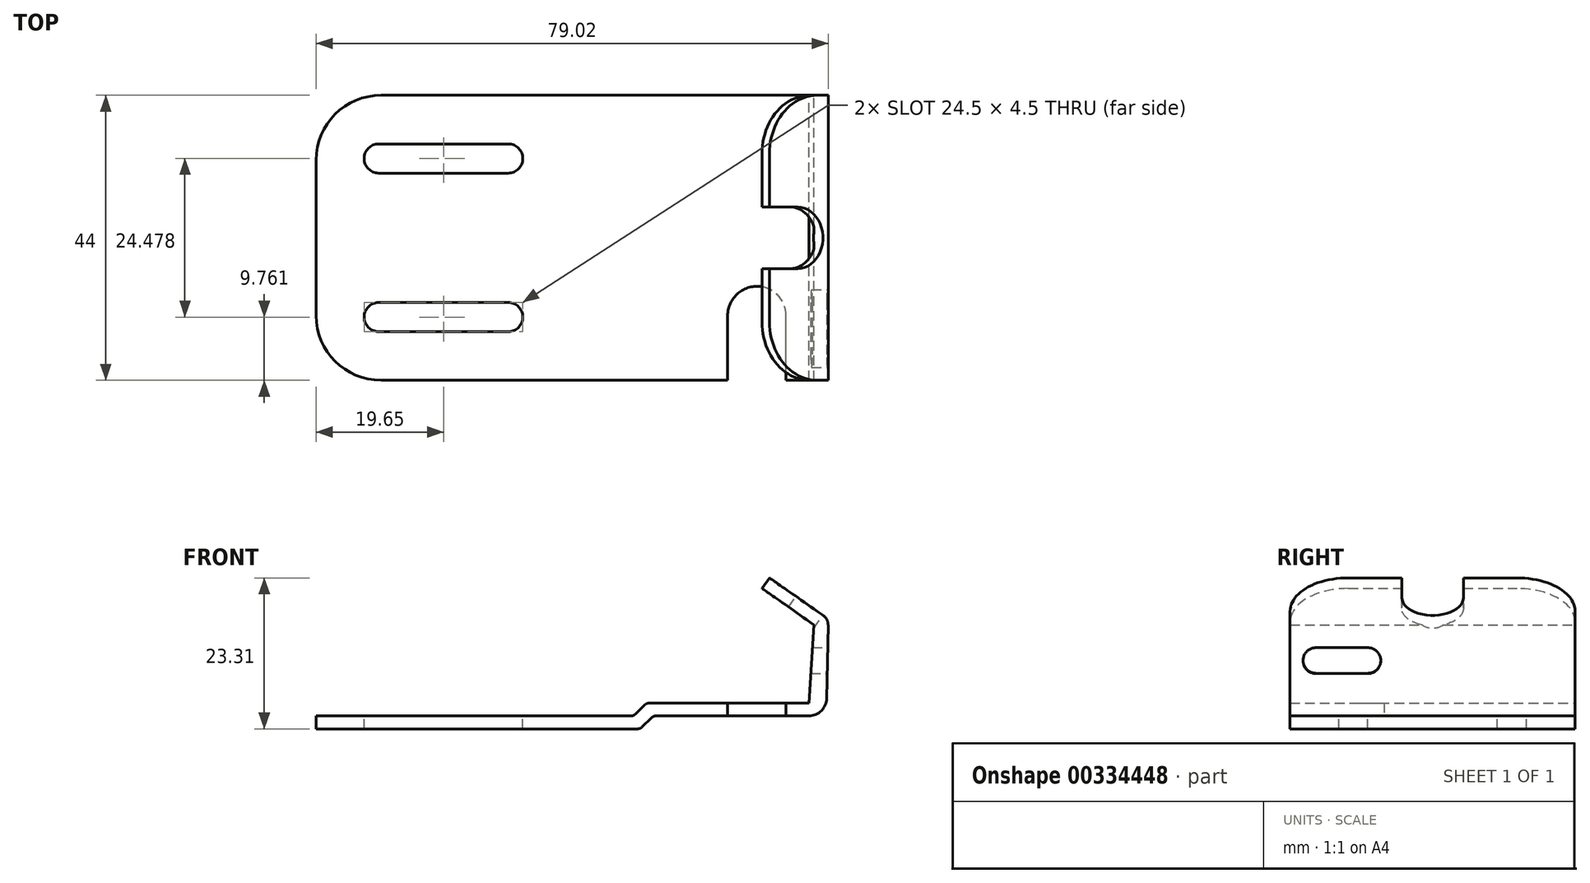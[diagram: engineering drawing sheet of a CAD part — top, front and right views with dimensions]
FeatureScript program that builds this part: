
annotation { "Feature Type Name" : "Feature", "Feature Type Description" : "" }
export const myFeature = defineFeature(function(context is Context, id is Id, definition is map)
    precondition{}
    {
        {
            var Q0;
            Q0=qCreatedBy(makeId("Front.planeOp"),FACE);
            var sketch = newSketch(context, id + "F0", { "sketchPlane" : qUnion([Q0])});
            skLineSegment(sketch, "E0", {"start": v(-0.4, 0) * mm, "end": v(-40, 0) * mm});
            skLineSegment(sketch, "E1", {"start": v(-40, 0) * mm, "end": v(-40, 2) * mm});
            skLineSegment(sketch, "E2", {"start": v(-40, 2) * mm, "end": v(-1.43, 2) * mm});
            skLineSegment(sketch, "E3", {"start": v(-0.73, 2.28) * mm, "end": v(0.75, 3.72) * mm});
            skLineSegment(sketch, "E4", {"start": v(1.44, 4) * mm, "end": v(26.04, 4) * mm});
            skLineSegment(sketch, "E5", {"start": v(0.3, 0.28) * mm, "end": v(1.77, 1.72) * mm});
            skLineSegment(sketch, "E6", {"start": v(2.46, 2) * mm, "end": v(26.04, 2) * mm});
            skPoint(sketch, "E7.visualSharp", {"position": v(-1.02, 2) * mm});
            skArc(sketch, "E7.filletArc", {"start": v(-1.43, 2) * mm, "mid": v(-1.05, 2.07) * mm, "end": v(-0.73, 2.28) * mm});
            skPoint(sketch, "E8.visualSharp", {"position": v(0, 0) * mm});
            skArc(sketch, "E8.filletArc", {"start": v(-0.4, 0) * mm, "mid": v(-0.03, 0.07) * mm, "end": v(0.3, 0.28) * mm});
            skPoint(sketch, "E9.visualSharp", {"position": v(2.06, 2) * mm});
            skArc(sketch, "E9.filletArc", {"start": v(2.46, 2) * mm, "mid": v(2.09, 1.93) * mm, "end": v(1.77, 1.72) * mm});
            skPoint(sketch, "E10.visualSharp", {"position": v(1.04, 4) * mm});
            skArc(sketch, "E10.filletArc", {"start": v(1.44, 4) * mm, "mid": v(1.07, 3.93) * mm, "end": v(0.75, 3.72) * mm});
            skLineSegment(sketch, "E11", {"start": v(26.04, 4) * mm, "end": v(26.83, 16.07) * mm});
            skLineSegment(sketch, "E12", {"start": v(26.83, 16.07) * mm, "end": v(26.19, 16.51) * mm});
            skLineSegment(sketch, "E13", {"start": v(26.19, 16.51) * mm, "end": v(27.33, 18.15) * mm});
            skLineSegment(sketch, "E14", {"start": v(27.33, 18.15) * mm, "end": v(28.27, 17.5) * mm});
            skArc(sketch, "E15", {"start": v(29.02, 16.03) * mm, "mid": v(28.83, 16.85) * mm, "end": v(28.27, 17.5) * mm});
            skLineSegment(sketch, "E16", {"start": v(29.02, 16.03) * mm, "end": v(28.8, 4.7) * mm});
            skArc(sketch, "E17", {"start": v(26.04, 2) * mm, "mid": v(27.97, 2.79) * mm, "end": v(28.8, 4.7) * mm});
            skSolve(sketch);
        }
        {
            var Q0;
            Q0=makeQuery(id+"F0.imprint","IMPRINT",FACE,{"disambiguationData":[TD([[makeQuery(id+"F0.imprint","IMPRINT",EDGE,{"derivedFrom":sQuery(id+"F0.wireOp",EDGE,"E0")}),-1.0]])]});
            extrude(context, id + "F1", {"entities" : qUnion([Q0]), "depth" : 44 * mm, "symmetric" : true});
        }
        {
            var Q0;
            Q0=makeQuery(id+"F1.opExtrude","SWEPT_FACE",FACE,{"disambiguationData":[OSD([sQuery(id+"F0.wireOp",EDGE,"E2")])]});
            var sketch = newSketch(context, id + "F2", { "sketchPlane" : qUnion([Q0])});
            skLineSegment(sketch, "E18", {"start": v(-50, -12) * mm, "end": v(-50, 12) * mm});
            skArc(sketch, "E19", {"start": v(-50, -12) * mm, "mid": v(-47.07, -19.07) * mm, "end": v(-40, -22) * mm});
            skArc(sketch, "E20", {"start": v(-50, 12) * mm, "mid": v(-47.07, 19.07) * mm, "end": v(-40, 22) * mm});
            skSolve(sketch);
        }
        {
            var Q0;
            Q0=makeQuery(id+"F2.imprint","IMPRINT",FACE,{"disambiguationData":[TD([[makeQuery(id+"F2.imprint","IMPRINT",EDGE,{"derivedFrom":sQuery(id+"F2.wireOp",EDGE,"E18")}),-1.0]])]});
            extrude(context, id + "F3", {"entities" : qUnion([Q0]), "operationType" : NewBodyOperationType.ADD, "oppositeDirection" : true, "depth" : 2 * mm});
        }
        {
            var Q0;
            {var subQ0=sQuery(id+"F0.wireOp",EDGE,"E2");Q0=makeQuery(id+"F3.boolean.opBoolean","MERGE",FACE,{"derivedFrom":[makeQuery(id+"F1.opExtrude","SWEPT_FACE",FACE,{"disambiguationData":[OSD([subQ0])]}),makeQuery(id+"F3.opExtrude","CAP_FACE",FACE,{"disambiguationData":[OSD([sQuery(id+"F0.wireOp",EDGE,"E1"),subQ0,sQuery(id+"F2.wireOp",EDGE,"E18"),sQuery(id+"F2.wireOp",EDGE,"E19"),sQuery(id+"F2.wireOp",EDGE,"E20")])],"isStart":true})]});}
            var sketch = newSketch(context, id + "F4", { "sketchPlane" : qUnion([Q0])});
            skLineSegment(sketch, "E21.bottom", {"start": v(-40.35, 9.99) * mm, "end": v(-20.35, 9.99) * mm});
            skLineSegment(sketch, "E21.top", {"start": v(-40.35, 14.49) * mm, "end": v(-20.35, 14.49) * mm});
            skArc(sketch, "E22", {"start": v(-40.35, 14.49) * mm, "mid": v(-42.6, 12.24) * mm, "end": v(-40.35, 9.99) * mm});
            skArc(sketch, "E23", {"start": v(-20.35, 9.99) * mm, "mid": v(-18.1, 12.24) * mm, "end": v(-20.35, 14.49) * mm});
            skLineSegment(sketch, "E24.MirrorCS", {"start": v(-40.35, -9.99) * mm, "end": v(-20.35, -9.99) * mm});
            skArc(sketch, "E25.MirrorCS", {"start": v(-40.35, -14.49) * mm, "mid": v(-42.6, -12.24) * mm, "end": v(-40.35, -9.99) * mm});
            skLineSegment(sketch, "E26.MirrorCS", {"start": v(-40.35, -14.49) * mm, "end": v(-20.35, -14.49) * mm});
            skArc(sketch, "E27.MirrorCS", {"start": v(-20.35, -9.99) * mm, "mid": v(-18.1, -12.24) * mm, "end": v(-20.35, -14.49) * mm});
            skSolve(sketch);
        }
        {
            var Q0;
            Q0=makeQuery(id+"F4.imprint","IMPRINT",FACE,{"disambiguationData":[TD([[makeQuery(id+"F4.imprint","IMPRINT",EDGE,{"derivedFrom":sQuery(id+"F4.wireOp",EDGE,"74778763-9d36-4775-81b6-88130280f72f0.MirrorCS")}),1.0]])]});
            var Q1;
            Q1=makeQuery(id+"F4.imprint","IMPRINT",FACE,{"disambiguationData":[TD([[makeQuery(id+"F4.imprint","IMPRINT",EDGE,{"derivedFrom":sQuery(id+"F4.wireOp",EDGE,"E21.bottom")}),1.0]])]});
            extrude(context, id + "F5", {"entities" : qUnion([Q0, Q1]), "operationType" : NewBodyOperationType.REMOVE, "oppositeDirection" : true, "depth" : 25 * mm});
        }
        {
            var Q0;
            Q0=makeQuery(id+"F1.opExtrude","SWEPT_FACE",FACE,{"disambiguationData":[OSD([sQuery(id+"F0.wireOp",EDGE,"E16")])]});
            var sketch = newSketch(context, id + "F6", { "sketchPlane" : qUnion([Q0])});
            skLineSegment(sketch, "E28.bottom", {"start": v(-18, 13.1) * mm, "end": v(-10, 13.1) * mm});
            skLineSegment(sketch, "E28.top", {"start": v(-18, 9.1) * mm, "end": v(-10, 9.1) * mm});
            skArc(sketch, "E29", {"start": v(-10, 9.1) * mm, "mid": v(-8, 11.1) * mm, "end": v(-10, 13.1) * mm});
            skArc(sketch, "E30", {"start": v(-18, 13.1) * mm, "mid": v(-20, 11.1) * mm, "end": v(-18, 9.1) * mm});
            skSolve(sketch);
        }
        {
            var Q0;
            Q0=makeQuery(id+"F6.imprint","IMPRINT",FACE,{"disambiguationData":[TD([[makeQuery(id+"F6.imprint","IMPRINT",EDGE,{"derivedFrom":sQuery(id+"F6.wireOp",EDGE,"E28.bottom")}),-1.0]])]});
            extrude(context, id + "F7", {"entities" : qUnion([Q0]), "operationType" : NewBodyOperationType.REMOVE, "oppositeDirection" : true, "depth" : 25 * mm});
        }
        {
            var Q0;
            Q0=makeQuery(id+"F1.opExtrude","SWEPT_FACE",FACE,{"disambiguationData":[OSD([sQuery(id+"F0.wireOp",EDGE,"E14")])]});
            var sketch = newSketch(context, id + "F8", { "sketchPlane" : qUnion([Q0])});
            skLineSegment(sketch, "E31", {"start": v(2.98, -13) * mm, "end": v(2.98, 13) * mm});
            skArc(sketch, "E32", {"start": v(2.98, -13) * mm, "mid": v(5.61, -19.36) * mm, "end": v(11.98, -22) * mm});
            skArc(sketch, "E33", {"start": v(2.98, 13) * mm, "mid": v(5.61, 19.36) * mm, "end": v(11.98, 22) * mm});
            skSolve(sketch);
        }
        {
            var Q0;
            Q0=makeQuery(id+"F8.imprint","IMPRINT",FACE,{"disambiguationData":[TD([[makeQuery(id+"F8.imprint","IMPRINT",EDGE,{"derivedFrom":sQuery(id+"F8.wireOp",EDGE,"E31")}),-1.0]])]});
            extrude(context, id + "F9", {"entities" : qUnion([Q0]), "operationType" : NewBodyOperationType.ADD, "oppositeDirection" : true, "depth" : 2 * mm});
        }
        {
            var Q0;
            {var subQ0=sQuery(id+"F0.wireOp",EDGE,"E14");Q0=makeQuery(id+"F9.boolean.opBoolean","MERGE",FACE,{"derivedFrom":[makeQuery(id+"F1.opExtrude","SWEPT_FACE",FACE,{"disambiguationData":[OSD([subQ0])]}),makeQuery(id+"F9.opExtrude","CAP_FACE",FACE,{"disambiguationData":[OSD([sQuery(id+"F0.wireOp",EDGE,"E13"),subQ0,sQuery(id+"F8.wireOp",EDGE,"E31"),sQuery(id+"F8.wireOp",EDGE,"E32"),sQuery(id+"F8.wireOp",EDGE,"E33")])],"isStart":true})]});}
            var sketch = newSketch(context, id + "F10", { "sketchPlane" : qUnion([Q0])});
            skLineSegment(sketch, "E34", {"start": v(2.98, 0) * mm, "end": v(13.12, 0) * mm, "construction": true});
            skLineSegment(sketch, "E35", {"start": v(2.98, -4.75) * mm, "end": v(7.98, -4.75) * mm});
            skLineSegment(sketch, "E36", {"start": v(2.98, 4.75) * mm, "end": v(7.98, 4.75) * mm});
            skArc(sketch, "E37", {"start": v(7.98, -4.75) * mm, "mid": v(13.06, 0) * mm, "end": v(7.98, 4.75) * mm});
            skSolve(sketch);
        }
        {
            var Q0;
            {var subQ0=sQuery(id+"F10.wireOp",EDGE,"E35");Q0=makeQuery(id+"F10.imprint","IMPRINT",FACE,{"disambiguationData":[TD([[makeQuery(id+"F10.imprint","IMPRINT",EDGE,{"derivedFrom":subQ0}),1.0]])]});}
            extrude(context, id + "F11", {"entities" : qUnion([Q0]), "operationType" : NewBodyOperationType.REMOVE, "endBound" : BoundingType.UP_TO_NEXT, "oppositeDirection" : true, "depth" : 25 * mm});
        }
        {
            var Q0;
            Q0=makeQuery(id+"F1.opExtrude","SWEPT_FACE",FACE,{"disambiguationData":[OSD([sQuery(id+"F0.wireOp",EDGE,"E6")])]});
            var sketch = newSketch(context, id + "F12", { "sketchPlane" : qUnion([Q0])});
            skLineSegment(sketch, "E38.bottom", {"start": v(22.52, 22) * mm, "end": v(13.52, 22) * mm});
            skLineSegment(sketch, "E38.left", {"start": v(22.52, 22) * mm, "end": v(22.52, 12) * mm});
            skLineSegment(sketch, "E38.right", {"start": v(13.52, 22) * mm, "end": v(13.52, 12) * mm});
            skArc(sketch, "E39", {"start": v(13.52, 12) * mm, "mid": v(18.02, 7.5) * mm, "end": v(22.52, 12) * mm});
            skSolve(sketch);
        }
        {
            var Q0;
            Q0=makeQuery(id+"F12.imprint","IMPRINT",FACE,{"disambiguationData":[TD([[makeQuery(id+"F12.imprint","IMPRINT",EDGE,{"derivedFrom":sQuery(id+"F12.wireOp",EDGE,"E38.bottom")}),-1.0]])]});
            extrude(context, id + "F13", {"entities" : qUnion([Q0]), "operationType" : NewBodyOperationType.REMOVE, "endBound" : BoundingType.UP_TO_NEXT, "oppositeDirection" : true, "depth" : 25 * mm});
        }
        {
            var Q0;
            Q0=makeQuery(id+"F4.imprint","IMPRINT",FACE,{"disambiguationData":[TD([[makeQuery(id+"F4.imprint","IMPRINT",EDGE,{"derivedFrom":sQuery(id+"F4.wireOp",EDGE,"E24.MirrorCS")}),-1.0]])]});
            extrude(context, id + "F14", {"entities" : qUnion([Q0]), "operationType" : NewBodyOperationType.REMOVE, "oppositeDirection" : true, "depth" : 25 * mm});
        }
    });
